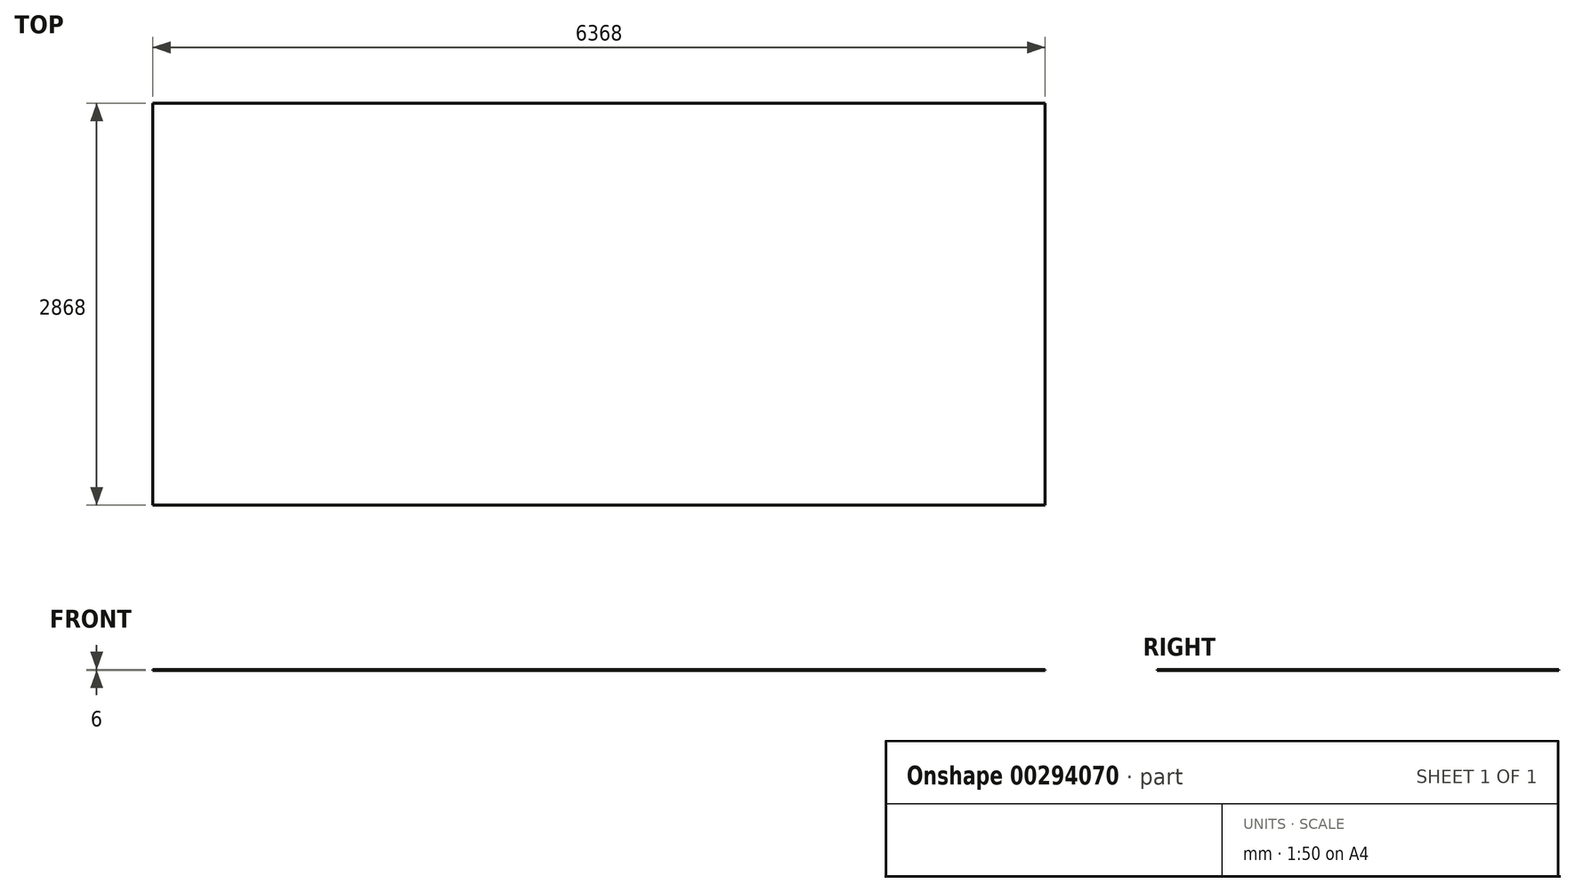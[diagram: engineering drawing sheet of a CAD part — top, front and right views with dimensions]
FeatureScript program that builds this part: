
annotation { "Feature Type Name" : "Feature", "Feature Type Description" : "" }
export const myFeature = defineFeature(function(context is Context, id is Id, definition is map)
    precondition{}
    {
        {
            var Q0;
            Q0=qCreatedBy(makeId("Top.planeOp"),FACE);
            var sketch = newSketch(context, id + "F0", { "sketchPlane" : qUnion([Q0])});
            skLineSegment(sketch, "E0", {"start": v(0, 0) * mm, "end": v(0, 2868) * mm});
            skLineSegment(sketch, "E1", {"start": v(0, 2868) * mm, "end": v(6368, 2868) * mm});
            skLineSegment(sketch, "E2", {"start": v(6368, 2868) * mm, "end": v(6368, 0) * mm});
            skLineSegment(sketch, "E3", {"start": v(6368, 0) * mm, "end": v(0, 0) * mm});
            skSolve(sketch);
        }
        {
            var Q0;
            Q0=makeQuery(id+"F0.imprint","IMPRINT",FACE,{"disambiguationData":[TD([[makeQuery(id+"F0.imprint","IMPRINT",EDGE,{"derivedFrom":sQuery(id+"F0.wireOp",EDGE,"E0")}),-1.0]])]});
            extrude(context, id + "F1", {"entities" : qUnion([Q0]), "depth" : 6 * mm});
        }
    });
